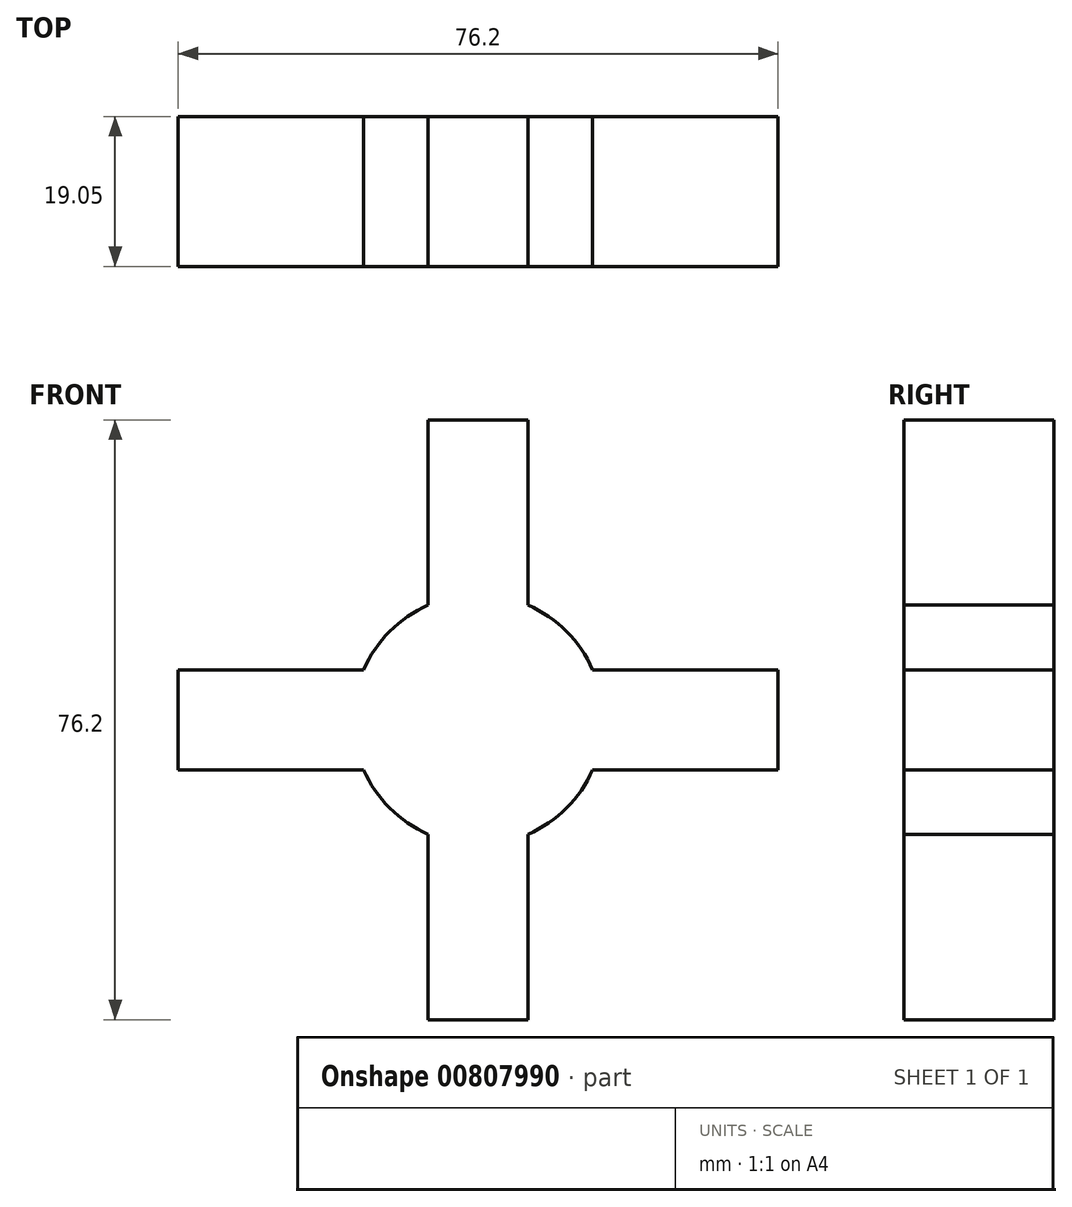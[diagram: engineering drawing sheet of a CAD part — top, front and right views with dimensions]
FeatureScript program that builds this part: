
annotation { "Feature Type Name" : "Feature", "Feature Type Description" : "" }
export const myFeature = defineFeature(function(context is Context, id is Id, definition is map)
    precondition{}
    {
        {
            var Q0;
            Q0=qCreatedBy(makeId("Front.planeOp"),FACE);
            var sketch = newSketch(context, id + "F0", { "sketchPlane" : qUnion([Q0])});
            skLineSegment(sketch, "E0.bottom", {"start": v(38.1, -38.1) * mm, "end": v(-38.1, -38.1) * mm});
            skLineSegment(sketch, "E0.top", {"start": v(38.1, 38.1) * mm, "end": v(-38.1, 38.1) * mm});
            skLineSegment(sketch, "E0.left", {"start": v(38.1, -38.1) * mm, "end": v(38.1, 38.1) * mm});
            skLineSegment(sketch, "E0.right", {"start": v(-38.1, -38.1) * mm, "end": v(-38.1, 38.1) * mm});
            skPoint(sketch, "E0.middle", {"position": v(0, 0) * mm});
            skSolve(sketch);
        }
        {
            var Q0;
            Q0=qCreatedBy(makeId("Front.planeOp"),FACE);
            var sketch = newSketch(context, id + "F1", { "sketchPlane" : qUnion([Q0])});
            skLineSegment(sketch, "E1", {"start": v(-38.1, 38.1) * mm, "end": v(-38.1, 6.35) * mm});
            skLineSegment(sketch, "E2", {"start": v(-38.1, 6.35) * mm, "end": v(-6.35, 6.35) * mm});
            skLineSegment(sketch, "E3", {"start": v(-6.35, 6.35) * mm, "end": v(-6.35, 38.1) * mm});
            skLineSegment(sketch, "E4", {"start": v(-38.1, 38.1) * mm, "end": v(-6.35, 38.1) * mm});
            skLineSegment(sketch, "E5", {"start": v(-38.1, -38.1) * mm, "end": v(-38.1, -6.35) * mm});
            skLineSegment(sketch, "E6", {"start": v(-38.1, -6.35) * mm, "end": v(-6.35, -6.35) * mm});
            skLineSegment(sketch, "E7", {"start": v(-6.35, -6.35) * mm, "end": v(-6.35, -38.1) * mm});
            skPoint(sketch, "E7.endSnap0", {"position": v(-19.05, -38.1) * mm});
            skLineSegment(sketch, "E8", {"start": v(-38.1, -38.1) * mm, "end": v(-6.35, -38.1) * mm});
            skLineSegment(sketch, "E9", {"start": v(38.1, -38.1) * mm, "end": v(38.1, -6.35) * mm});
            skLineSegment(sketch, "E10", {"start": v(38.1, -6.35) * mm, "end": v(6.35, -6.35) * mm});
            skLineSegment(sketch, "E11", {"start": v(6.35, -6.35) * mm, "end": v(6.35, -38.1) * mm});
            skLineSegment(sketch, "E12", {"start": v(6.35, -38.1) * mm, "end": v(38.1, -38.1) * mm});
            skLineSegment(sketch, "E13", {"start": v(38.1, 38.1) * mm, "end": v(6.35, 38.1) * mm});
            skLineSegment(sketch, "E14", {"start": v(6.35, 38.1) * mm, "end": v(6.35, 6.35) * mm});
            skLineSegment(sketch, "E15", {"start": v(6.35, 6.35) * mm, "end": v(38.1, 6.35) * mm});
            skLineSegment(sketch, "E16", {"start": v(38.1, 6.35) * mm, "end": v(38.1, 38.1) * mm});
            skSolve(sketch);
        }
        {
            var Q0;
            Q0=makeQuery(id+"F0.imprint","IMPRINT",FACE,{"disambiguationData":[TD([[makeQuery(id+"F0.imprint","IMPRINT",EDGE,{"derivedFrom":sQuery(id+"F0.wireOp",EDGE,"E0.bottom")}),-1.0]])]});
            extrude(context, id + "F2", {"entities" : qUnion([Q0]), "depth" : 19.05 * mm, "offsetDistance" : 25.4 * mm});
        }
        {
            var Q0;
            Q0 = qSketchRegion(id + "F1", true);
            extrude(context, id + "F3", {"entities" : qUnion([Q0]), "operationType" : NewBodyOperationType.REMOVE, "endBound" : BoundingType.THROUGH_ALL, "depth" : 25.4 * mm, "offsetDistance" : 25.4 * mm});
        }
        {
            var Q0;
            Q0=qCreatedBy(makeId("Front.planeOp"),FACE);
            var sketch = newSketch(context, id + "F4", { "sketchPlane" : qUnion([Q0])});
            skCircle(sketch, "E17", {"center": v(0, 0) * mm, "radius": 15.88 * mm});
            skSolve(sketch);
        }
        {
            var Q0;
            Q0 = qSketchRegion(id + "F4", true);
            extrude(context, id + "F5", {"entities" : qUnion([Q0]), "operationType" : NewBodyOperationType.ADD, "depth" : 19.05 * mm, "offsetDistance" : 25.4 * mm});
        }
    });
